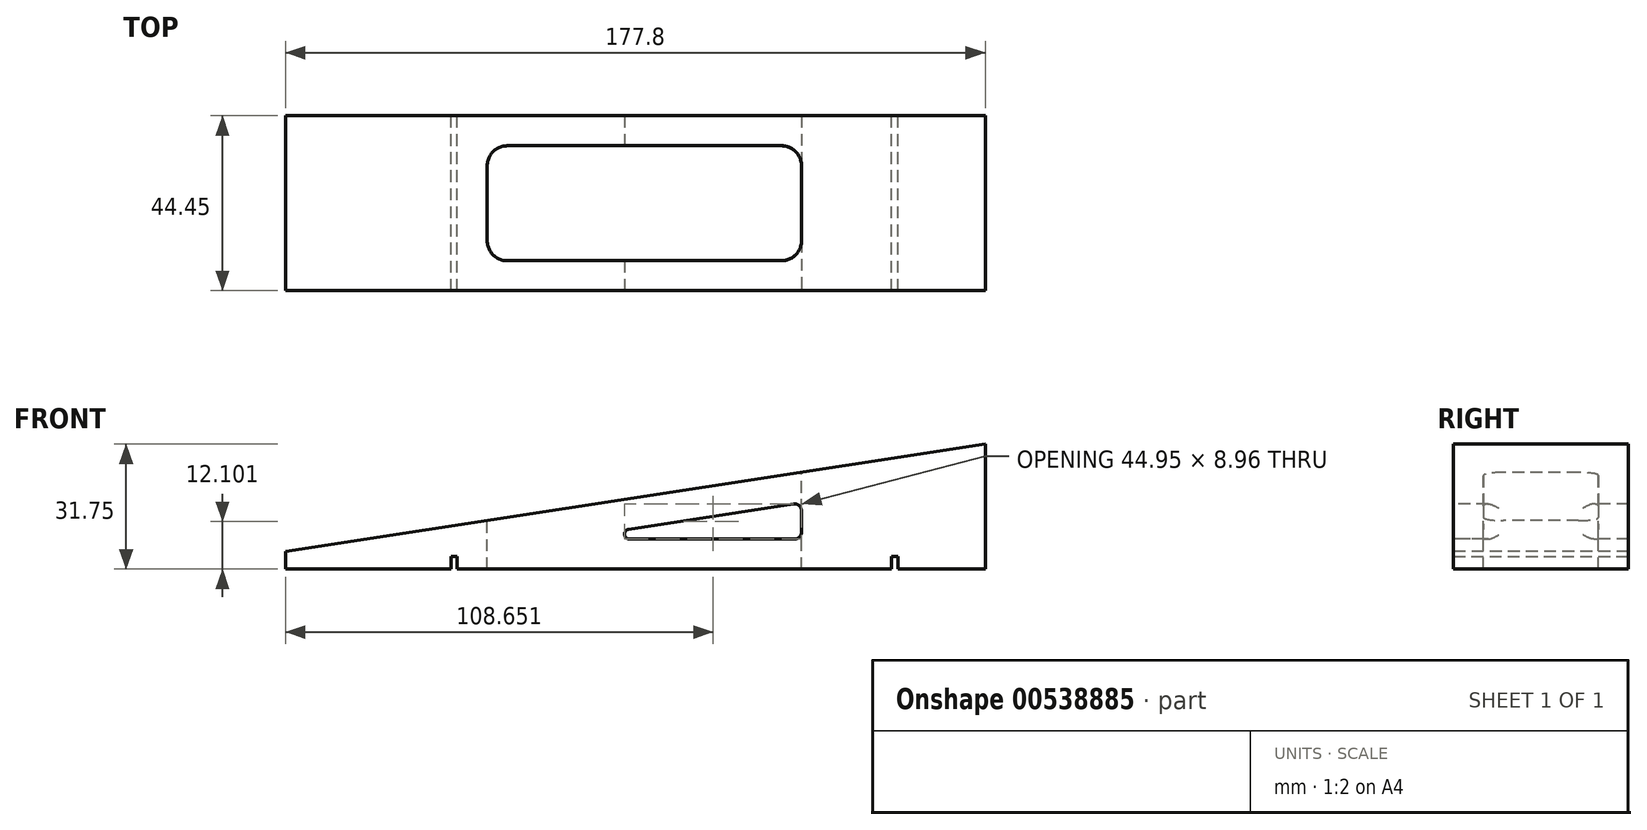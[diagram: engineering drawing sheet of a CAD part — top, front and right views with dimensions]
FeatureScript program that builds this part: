
annotation { "Feature Type Name" : "Feature", "Feature Type Description" : "" }
export const myFeature = defineFeature(function(context is Context, id is Id, definition is map)
    precondition{}
    {
        {
            var Q0;
            Q0=qCreatedBy(makeId("Top.planeOp"),FACE);
            var sketch = newSketch(context, id + "F0", { "sketchPlane" : qUnion([Q0])});
            skLineSegment(sketch, "E0.bottom", {"start": v(0, 0) * mm, "end": v(-177.8, 0) * mm});
            skLineSegment(sketch, "E0.top", {"start": v(0, -44.45) * mm, "end": v(-177.8, -44.45) * mm});
            skLineSegment(sketch, "E0.left", {"start": v(0, 0) * mm, "end": v(0, -44.45) * mm});
            skLineSegment(sketch, "E0.right", {"start": v(-177.8, 0) * mm, "end": v(-177.8, -44.45) * mm});
            skSolve(sketch);
        }
        {
            var Q0;
            Q0=makeQuery(id+"F0.imprint","IMPRINT",FACE,{"disambiguationData":[TD([[makeQuery(id+"F0.imprint","IMPRINT",EDGE,{"derivedFrom":sQuery(id+"F0.wireOp",EDGE,"E0.bottom")}),1.0]])]});
            extrude(context, id + "F1", {"entities" : qUnion([Q0]), "depth" : 31.75 * mm});
        }
        {
            var Q0;
            Q0=makeQuery(id+"F1.opExtrude","CAP_FACE",FACE,{"disambiguationData":[OSD([sQuery(id+"F0.wireOp",EDGE,"E0.bottom"),sQuery(id+"F0.wireOp",EDGE,"E0.top"),sQuery(id+"F0.wireOp",EDGE,"E0.left"),sQuery(id+"F0.wireOp",EDGE,"E0.right")])],"isStart":true});
            var sketch = newSketch(context, id + "F2", { "sketchPlane" : qUnion([Q0])});
            skLineSegment(sketch, "E1.bottom", {"start": v(-135.73, 44.45) * mm, "end": v(-134.14, 44.45) * mm});
            skLineSegment(sketch, "E1.top", {"start": v(-135.73, 0) * mm, "end": v(-134.14, 0) * mm});
            skLineSegment(sketch, "E1.left", {"start": v(-135.73, 44.45) * mm, "end": v(-135.73, 0) * mm});
            skLineSegment(sketch, "E1.right", {"start": v(-134.14, 44.45) * mm, "end": v(-134.14, 0) * mm});
            skLineSegment(sketch, "E2.bottom", {"start": v(-23.81, 44.45) * mm, "end": v(-22.23, 44.45) * mm});
            skLineSegment(sketch, "E2.top", {"start": v(-23.81, 0) * mm, "end": v(-22.23, 0) * mm});
            skLineSegment(sketch, "E2.left", {"start": v(-23.81, 44.45) * mm, "end": v(-23.81, 0) * mm});
            skLineSegment(sketch, "E2.right", {"start": v(-22.23, 44.45) * mm, "end": v(-22.23, 0) * mm});
            skSolve(sketch);
        }
        {
            var Q0;
            Q0=makeQuery(id+"F2.imprint","IMPRINT",FACE,{"disambiguationData":[TD([[makeQuery(id+"F2.imprint","IMPRINT",EDGE,{"derivedFrom":sQuery(id+"F2.wireOp",EDGE,"E2.bottom")}),1.0]])]});
            var Q1;
            Q1=makeQuery(id+"F2.imprint","IMPRINT",FACE,{"disambiguationData":[TD([[makeQuery(id+"F2.imprint","IMPRINT",EDGE,{"derivedFrom":sQuery(id+"F2.wireOp",EDGE,"E1.bottom")}),1.0]])]});
            extrude(context, id + "F3", {"entities" : qUnion([Q0, Q1]), "operationType" : NewBodyOperationType.REMOVE, "oppositeDirection" : true, "depth" : 3.17 * mm});
        }
        {
            var Q0;
            Q0=makeQuery(id+"F1.opExtrude","CAP_FACE",FACE,{"disambiguationData":[OSD([sQuery(id+"F0.wireOp",EDGE,"E0.bottom"),sQuery(id+"F0.wireOp",EDGE,"E0.top"),sQuery(id+"F0.wireOp",EDGE,"E0.left"),sQuery(id+"F0.wireOp",EDGE,"E0.right")])],"isStart":false});
            var sketch = newSketch(context, id + "F4", { "sketchPlane" : qUnion([Q0])});
            skLineSegment(sketch, "E3.bottom", {"start": v(-46.67, -7.62) * mm, "end": v(-126.52, -7.62) * mm});
            skLineSegment(sketch, "E3.top", {"start": v(-46.67, -36.83) * mm, "end": v(-126.52, -36.83) * mm});
            skLineSegment(sketch, "E3.left", {"start": v(-46.67, -7.62) * mm, "end": v(-46.67, -36.83) * mm});
            skLineSegment(sketch, "E3.right", {"start": v(-126.52, -7.62) * mm, "end": v(-126.52, -36.83) * mm});
            skSolve(sketch);
        }
        {
            var Q0;
            Q0=makeQuery(id+"F4.imprint","IMPRINT",FACE,{"disambiguationData":[TD([[makeQuery(id+"F4.imprint","IMPRINT",EDGE,{"derivedFrom":sQuery(id+"F4.wireOp",EDGE,"E3.bottom")}),1.0]])]});
            extrude(context, id + "F5", {"entities" : qUnion([Q0]), "operationType" : NewBodyOperationType.REMOVE, "endBound" : BoundingType.THROUGH_ALL, "oppositeDirection" : true, "depth" : 25.4 * mm, "offsetDistance" : 25.4 * mm});
        }
        {
            var Q0;
            Q0=makeQuery(id+"F1.opExtrude","SWEPT_FACE",FACE,{"disambiguationData":[OSD([sQuery(id+"F0.wireOp",EDGE,"E0.top")])]});
            var sketch = newSketch(context, id + "F6", { "sketchPlane" : qUnion([Q0])});
            skLineSegment(sketch, "E4", {"start": v(-177.8, 4.47) * mm, "end": v(0, 31.75) * mm});
            skLineSegment(sketch, "E5", {"start": v(0, 31.75) * mm, "end": v(-177.8, 31.75) * mm});
            skLineSegment(sketch, "E6", {"start": v(-177.8, 31.75) * mm, "end": v(-177.8, 4.47) * mm});
            skSolve(sketch);
        }
        {
            var Q0;
            Q0=qSketchRegion(id+"F6",true);
            extrude(context, id + "F7", {"entities" : qUnion([Q0]), "operationType" : NewBodyOperationType.REMOVE, "endBound" : BoundingType.THROUGH_ALL, "oppositeDirection" : true, "depth" : 25.4 * mm, "offsetDistance" : 25.4 * mm});
        }
        {
            var Q0;
            Q0=makeQuery(id+"F5.boolean.opBoolean","COPY",EDGE,{"derivedFrom":makeQuery(id+"F5.opExtrude","SWEPT_EDGE",EDGE,{"disambiguationData":[OSD([sQuery(id+"F4.wireOp",EDGE,"E3.bottom"),sQuery(id+"F4.wireOp",EDGE,"E3.right")])]})});
            var Q1;
            Q1=makeQuery(id+"F5.boolean.opBoolean","COPY",EDGE,{"derivedFrom":makeQuery(id+"F5.opExtrude","SWEPT_EDGE",EDGE,{"disambiguationData":[OSD([sQuery(id+"F4.wireOp",EDGE,"E3.bottom"),sQuery(id+"F4.wireOp",EDGE,"E3.left")])]})});
            var Q2;
            Q2=makeQuery(id+"F5.boolean.opBoolean","COPY",EDGE,{"derivedFrom":makeQuery(id+"F5.opExtrude","SWEPT_EDGE",EDGE,{"disambiguationData":[OSD([sQuery(id+"F4.wireOp",EDGE,"E3.top"),sQuery(id+"F4.wireOp",EDGE,"E3.right")])]})});
            var Q3;
            Q3=makeQuery(id+"F5.boolean.opBoolean","COPY",EDGE,{"derivedFrom":makeQuery(id+"F5.opExtrude","SWEPT_EDGE",EDGE,{"disambiguationData":[OSD([sQuery(id+"F4.wireOp",EDGE,"E3.top"),sQuery(id+"F4.wireOp",EDGE,"E3.left")])]})});
            fillet(context, id + "F8", {"entities" : qUnion([Q0, Q1, Q2, Q3]), "radius" : 5.08 * mm, "tangentPropagation" : true, "allowEdgeOverflow" : false});
        }
        {
            var Q0;
            Q0=makeQuery(id+"F1.opExtrude","SWEPT_FACE",FACE,{"disambiguationData":[OSD([sQuery(id+"F0.wireOp",EDGE,"E0.top")])]});
            var sketch = newSketch(context, id + "F9", { "sketchPlane" : qUnion([Q0])});
            skLineSegment(sketch, "E7", {"start": v(-90.55, 10.15) * mm, "end": v(-48.72, 16.56) * mm});
            skLineSegment(sketch, "E8", {"start": v(-46.67, 14.8) * mm, "end": v(-46.67, 9.4) * mm});
            skLineSegment(sketch, "E9", {"start": v(-48.45, 7.62) * mm, "end": v(-90.36, 7.62) * mm});
            skPoint(sketch, "E10.visualSharp", {"position": v(-46.67, 16.88) * mm});
            skArc(sketch, "E10.filletArc", {"start": v(-46.67, 14.8) * mm, "mid": v(-47.3, 16.16) * mm, "end": v(-48.72, 16.56) * mm});
            skPoint(sketch, "E11.visualSharp", {"position": v(-46.67, 7.62) * mm});
            skArc(sketch, "E11.filletArc", {"start": v(-48.45, 7.62) * mm, "mid": v(-47.2, 8.14) * mm, "end": v(-46.67, 9.4) * mm});
            skPoint(sketch, "E12.visualSharp", {"position": v(-107, 7.62) * mm});
            skArc(sketch, "E12.filletArc", {"start": v(-90.55, 10.15) * mm, "mid": v(-91.63, 8.8) * mm, "end": v(-90.36, 7.62) * mm});
            skSolve(sketch);
        }
        {
            var Q0;
            Q0=makeQuery(id+"F9.imprint","IMPRINT",FACE,{"disambiguationData":[TD([[makeQuery(id+"F9.imprint","IMPRINT",EDGE,{"derivedFrom":sQuery(id+"F9.wireOp",EDGE,"E7")}),-1.0]])]});
            extrude(context, id + "F10", {"entities" : qUnion([Q0]), "operationType" : NewBodyOperationType.REMOVE, "endBound" : BoundingType.THROUGH_ALL, "oppositeDirection" : true, "depth" : 25.4 * mm, "offsetDistance" : 25.4 * mm});
        }
    });
